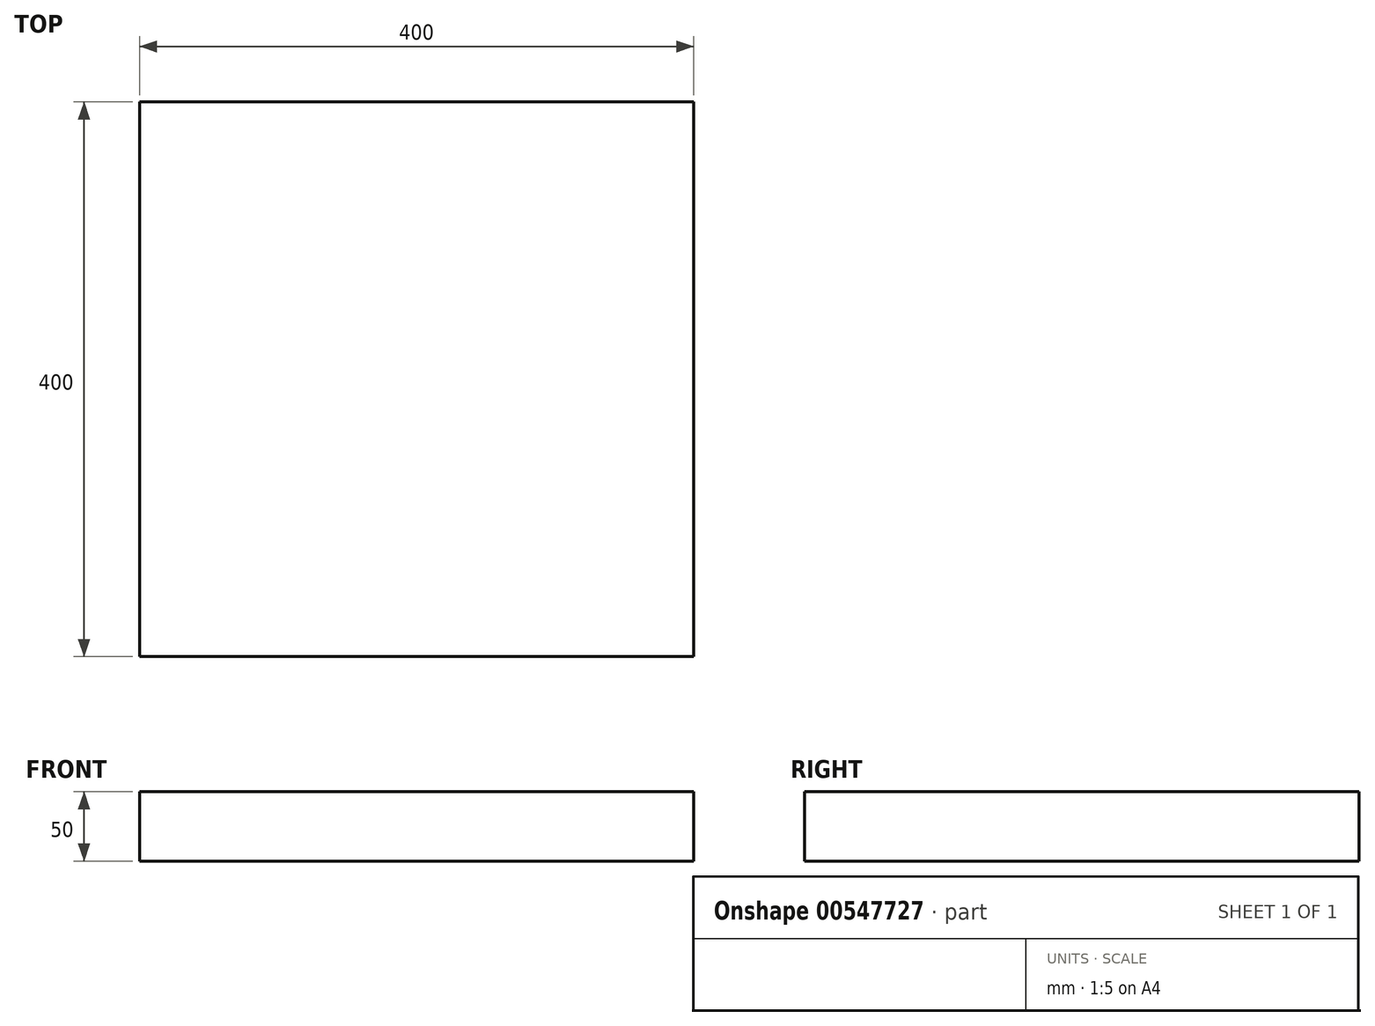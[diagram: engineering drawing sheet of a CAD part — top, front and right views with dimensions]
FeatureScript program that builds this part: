
annotation { "Feature Type Name" : "Feature", "Feature Type Description" : "" }
export const myFeature = defineFeature(function(context is Context, id is Id, definition is map)
    precondition{}
    {
        {
            var Q0;
            Q0=qCreatedBy(makeId("Top.planeOp"),FACE);
            var sketch = newSketch(context, id + "F0", { "sketchPlane" : qUnion([Q0])});
            skLineSegment(sketch, "E0.bottom", {"start": v(200, 200) * mm, "end": v(-200, 200) * mm});
            skLineSegment(sketch, "E0.top", {"start": v(200, -200) * mm, "end": v(-200, -200) * mm});
            skLineSegment(sketch, "E0.left", {"start": v(200, 200) * mm, "end": v(200, -200) * mm});
            skLineSegment(sketch, "E0.right", {"start": v(-200, 200) * mm, "end": v(-200, -200) * mm});
            skPoint(sketch, "E0.middle", {"position": v(0, 0) * mm});
            skLineSegment(sketch, "E1.bottom", {"start": v(-25, -75) * mm, "end": v(-175, -75) * mm});
            skLineSegment(sketch, "E1.top", {"start": v(-25, 75) * mm, "end": v(-175, 75) * mm});
            skLineSegment(sketch, "E1.right", {"start": v(-200, -75) * mm, "end": v(-200, 75) * mm});
            skLineSegment(sketch, "E2.bottom", {"start": v(-175, 175) * mm, "end": v(0, 175) * mm});
            skLineSegment(sketch, "E2.top", {"start": v(-175, 125) * mm, "end": v(0, 125) * mm});
            skLineSegment(sketch, "E2.left", {"start": v(-175, 175) * mm, "end": v(-175, 125) * mm});
            skLineSegment(sketch, "E2.right", {"start": v(0, 175) * mm, "end": v(0, 125) * mm});
            skLineSegment(sketch, "E3.bottom", {"start": v(-175, -125) * mm, "end": v(0, -125) * mm});
            skLineSegment(sketch, "E3.top", {"start": v(-175, -175) * mm, "end": v(0, -175) * mm});
            skLineSegment(sketch, "E3.left", {"start": v(-175, -125) * mm, "end": v(-175, -175) * mm});
            skLineSegment(sketch, "E3.right", {"start": v(0, -125) * mm, "end": v(0, -175) * mm});
            skLineSegment(sketch, "E4.bottom", {"start": v(25, 175) * mm, "end": v(175, 175) * mm});
            skLineSegment(sketch, "E4.top", {"start": v(25, 25) * mm, "end": v(175, 25) * mm});
            skLineSegment(sketch, "E4.left", {"start": v(25, 175) * mm, "end": v(25, 25) * mm});
            skLineSegment(sketch, "E4.right", {"start": v(175, 175) * mm, "end": v(175, 25) * mm});
            skLineSegment(sketch, "E5.bottom", {"start": v(25, -25) * mm, "end": v(175, -25) * mm});
            skLineSegment(sketch, "E5.top", {"start": v(25, -175) * mm, "end": v(175, -175) * mm});
            skLineSegment(sketch, "E5.left", {"start": v(25, -25) * mm, "end": v(25, -175) * mm});
            skLineSegment(sketch, "E5.right", {"start": v(175, -25) * mm, "end": v(175, -175) * mm});
            skLineSegment(sketch, "E6", {"start": v(-175, 75) * mm, "end": v(-175, -75) * mm});
            skLineSegment(sketch, "E7", {"start": v(-25, 75) * mm, "end": v(-25, -75) * mm});
            skSolve(sketch);
        }
        {
            var Q0;
            {var subQ1=sQuery(id+"F0.wireOp",EDGE,"E0.bottom");Q0=makeQuery(id+"F0.imprint","IMPRINT",FACE,{"disambiguationData":[TD([[makeQuery(id+"F0.imprint","IMPRINT",EDGE,{"derivedFrom":subQ1}),1.0]])]});}
            var Q1;
            Q1=makeQuery(id+"F0.imprint","IMPRINT",FACE,{"disambiguationData":[TD([[makeQuery(id+"F0.imprint","IMPRINT",EDGE,{"derivedFrom":sQuery(id+"F0.wireOp",EDGE,"E1.bottom")}),-1.0]])]});
            var Q2;
            Q2=makeQuery(id+"F0.imprint","IMPRINT",FACE,{"disambiguationData":[TD([[makeQuery(id+"F0.imprint","IMPRINT",EDGE,{"derivedFrom":sQuery(id+"F0.wireOp",EDGE,"E3.bottom")}),-1.0]])]});
            var Q3;
            Q3=makeQuery(id+"F0.imprint","IMPRINT",FACE,{"disambiguationData":[TD([[makeQuery(id+"F0.imprint","IMPRINT",EDGE,{"derivedFrom":sQuery(id+"F0.wireOp",EDGE,"E5.bottom")}),-1.0]])]});
            var Q4;
            Q4=makeQuery(id+"F0.imprint","IMPRINT",FACE,{"disambiguationData":[TD([[makeQuery(id+"F0.imprint","IMPRINT",EDGE,{"derivedFrom":sQuery(id+"F0.wireOp",EDGE,"E4.bottom")}),-1.0]])]});
            var Q5;
            Q5=makeQuery(id+"F0.imprint","IMPRINT",FACE,{"disambiguationData":[TD([[makeQuery(id+"F0.imprint","IMPRINT",EDGE,{"derivedFrom":sQuery(id+"F0.wireOp",EDGE,"E2.bottom")}),-1.0]])]});
            extrude(context, id + "F1", {"entities" : qUnion([Q0, Q1, Q2, Q3, Q4, Q5]), "depth" : 50 * mm, "offsetDistance" : 25 * mm});
        }
    });
